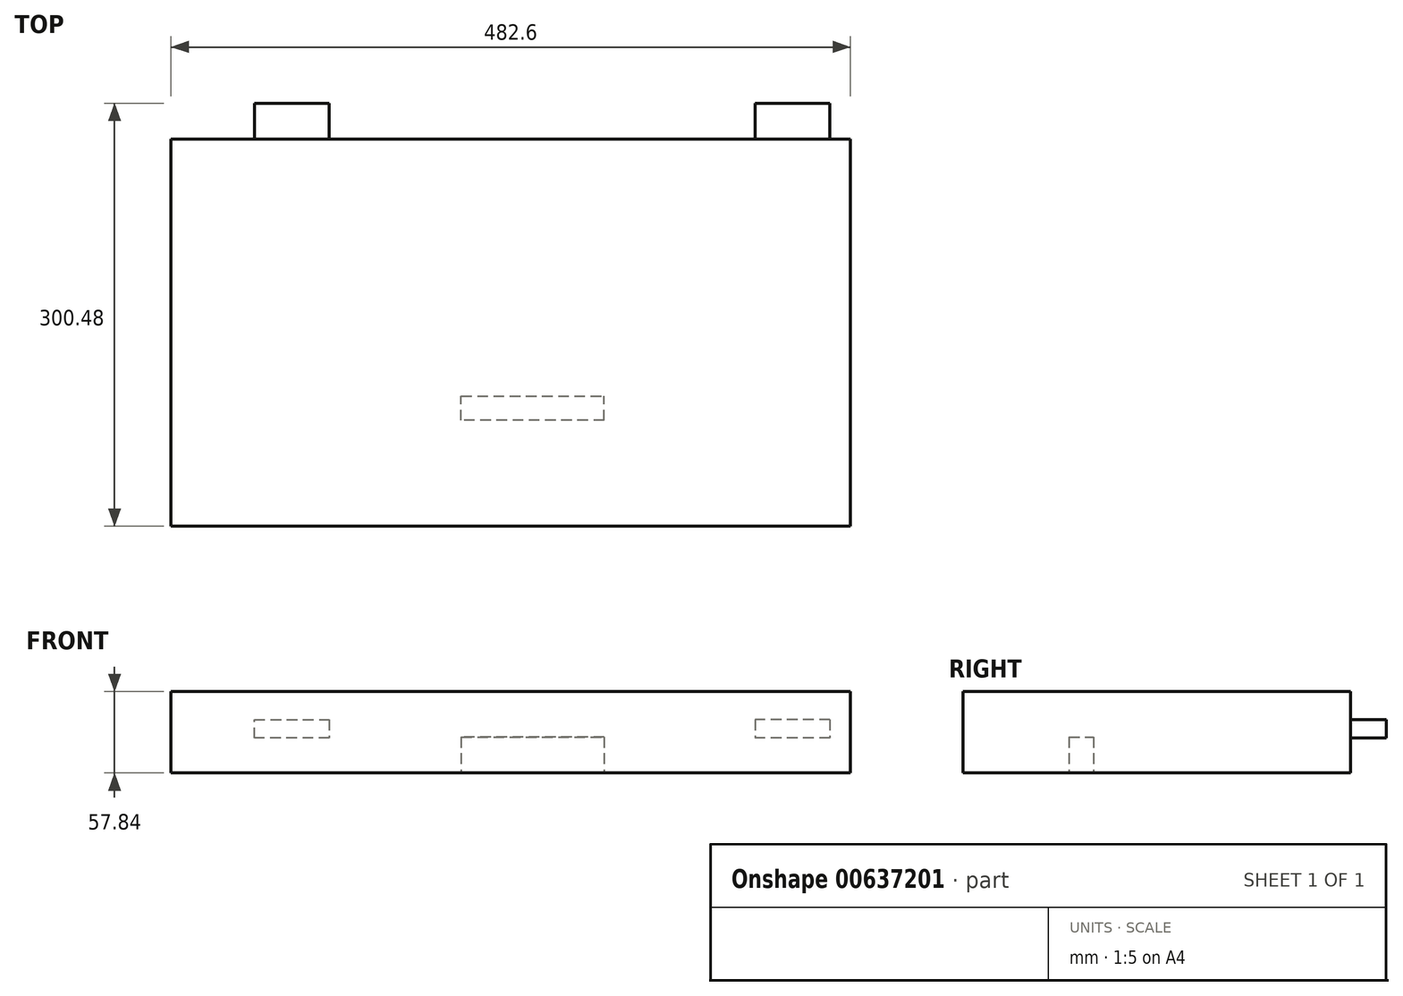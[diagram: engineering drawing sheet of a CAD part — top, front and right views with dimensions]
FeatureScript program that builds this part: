
annotation { "Feature Type Name" : "Feature", "Feature Type Description" : "" }
export const myFeature = defineFeature(function(context is Context, id is Id, definition is map)
    precondition{}
    {
        {
            var Q0;
            Q0=qCreatedBy(makeId("Front.planeOp"),FACE);
            var sketch = newSketch(context, id + "F0", { "sketchPlane" : qUnion([Q0])});
            skLineSegment(sketch, "E0", {"start": v(-270.03, 57.84) * mm, "end": v(212.57, 57.84) * mm});
            skLineSegment(sketch, "E1", {"start": v(-270.03, 57.84) * mm, "end": v(-270.03, 0) * mm});
            skLineSegment(sketch, "E2", {"start": v(-270.03, 0) * mm, "end": v(212.57, 0) * mm});
            skLineSegment(sketch, "E3", {"start": v(212.57, 0) * mm, "end": v(212.57, 57.84) * mm});
            skSolve(sketch);
        }
        {
            var Q0;
            Q0 = qSketchRegion(id + "F0", true);
            extrude(context, id + "F1", {"entities" : qUnion([Q0]), "depth" : 275.08 * mm, "offsetDistance" : 25.4 * mm});
        }
        {
            var Q0;
            Q0=makeQuery(id+"F1.opExtrude","CAP_FACE",FACE,{"disambiguationData":[OSD([sQuery(id+"F0.wireOp",EDGE,"E0"),sQuery(id+"F0.wireOp",EDGE,"E1"),sQuery(id+"F0.wireOp",EDGE,"E2"),sQuery(id+"F0.wireOp",EDGE,"E3")])],"isStart":true});
            var sketch = newSketch(context, id + "F2", { "sketchPlane" : qUnion([Q0])});
            skLineSegment(sketch, "E4", {"start": v(-197.98, 37.87) * mm, "end": v(-197.98, 24.8) * mm});
            skLineSegment(sketch, "E5", {"start": v(-197.98, 37.87) * mm, "end": v(-144.8, 37.87) * mm});
            skLineSegment(sketch, "E6", {"start": v(-144.8, 37.87) * mm, "end": v(-144.8, 24.8) * mm});
            skLineSegment(sketch, "E7", {"start": v(-197.98, 24.8) * mm, "end": v(-176.19, 24.8) * mm});
            skLineSegment(sketch, "E8", {"start": v(-144.8, 24.8) * mm, "end": v(-176.19, 24.8) * mm});
            skLineSegment(sketch, "E9", {"start": v(157.62, 37.87) * mm, "end": v(157.62, 24.8) * mm});
            skLineSegment(sketch, "E10", {"start": v(157.62, 24.8) * mm, "end": v(210.8, 24.8) * mm});
            skLineSegment(sketch, "E11", {"start": v(210.8, 24.8) * mm, "end": v(210.8, 37.87) * mm});
            skLineSegment(sketch, "E12", {"start": v(210.8, 37.87) * mm, "end": v(157.62, 37.87) * mm});
            skSolve(sketch);
        }
        {
            var Q0;
            Q0 = qSketchRegion(id + "F2", true);
            extrude(context, id + "F3", {"entities" : qUnion([Q0]), "operationType" : NewBodyOperationType.ADD, "depth" : 25.4 * mm, "offsetDistance" : 25.4 * mm});
        }
        {
            var Q0;
            Q0=makeQuery(id+"F3.boolean.opBoolean","MERGE",FACE,{"derivedFrom":[makeQuery(id+"F1.opExtrude","SWEPT_FACE",FACE,{"disambiguationData":[OSD([sQuery(id+"F0.wireOp",EDGE,"E2")])]}),makeQuery(id+"F3.opExtrude","SWEPT_FACE",FACE,{"disambiguationData":[OSD([sQuery(id+"F2.wireOp",EDGE,"zc0zWHkI-2pN6-MPK5-4OfL-LZMwvo3wDMUS")])]}),makeQuery(id+"F3.opExtrude","SWEPT_FACE",FACE,{"disambiguationData":[OSD([sQuery(id+"F2.wireOp",EDGE,"0INKRkWv-x6J0-0nOp-RDio-Mq98TiKZbp4P")])]})]});
            var sketch = newSketch(context, id + "F4", { "sketchPlane" : qUnion([Q0])});
            skLineSegment(sketch, "E13", {"start": v(-63.97, 182.56) * mm, "end": v(37.5, 182.56) * mm});
            skLineSegment(sketch, "E14", {"start": v(37.63, 199.91) * mm, "end": v(-63.97, 199.91) * mm});
            skLineSegment(sketch, "E15", {"start": v(-63.97, 199.91) * mm, "end": v(-63.97, 182.56) * mm});
            skLineSegment(sketch, "E16", {"start": v(37.63, 199.91) * mm, "end": v(37.5, 182.56) * mm});
            skSolve(sketch);
        }
        {
            var Q0;
            Q0 = qSketchRegion(id + "F4", true);
            extrude(context, id + "F5", {"entities" : qUnion([Q0]), "operationType" : NewBodyOperationType.REMOVE, "oppositeDirection" : true, "depth" : 25.4 * mm, "offsetDistance" : 25.4 * mm});
        }
    });
